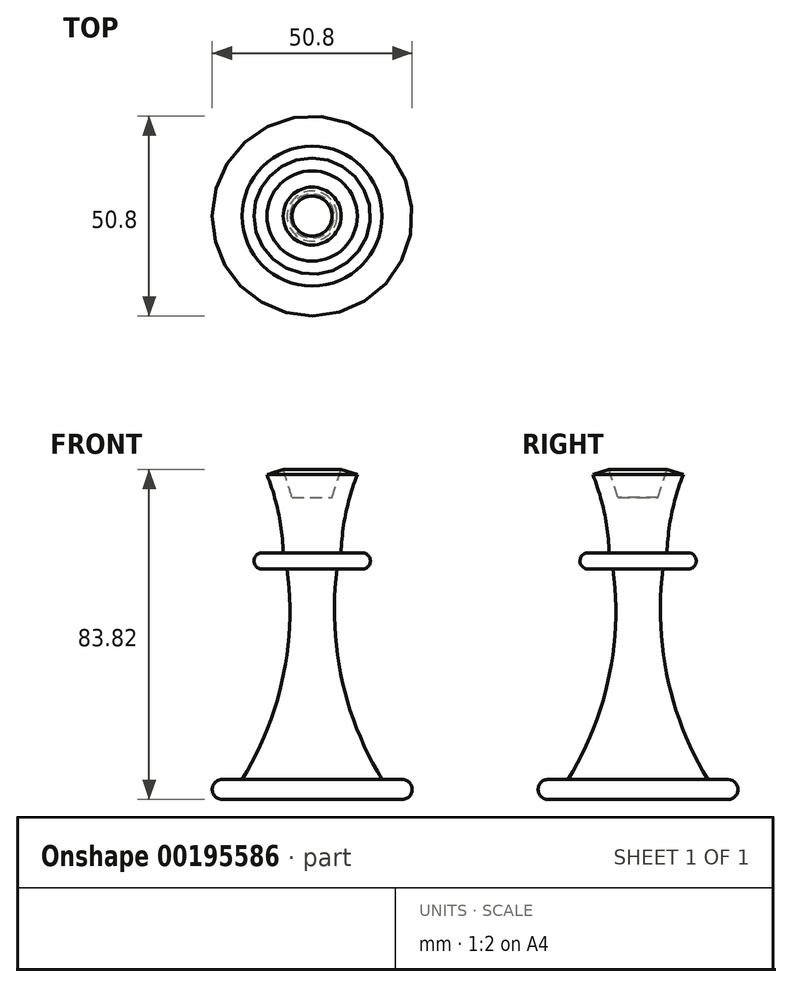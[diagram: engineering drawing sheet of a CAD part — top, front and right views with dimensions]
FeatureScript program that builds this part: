
annotation { "Feature Type Name" : "Feature", "Feature Type Description" : "" }
export const myFeature = defineFeature(function(context is Context, id is Id, definition is map)
    precondition{}
    {
        {
            var Q0;
            Q0=qCreatedBy(makeId("Front.planeOp"),FACE);
            var sketch = newSketch(context, id + "F0", { "sketchPlane" : qUnion([Q0])});
            skLineSegment(sketch, "E0", {"start": v(0, 0) * mm, "end": v(0, 83.82) * mm});
            skLineSegment(sketch, "E1", {"start": v(0, 0) * mm, "end": v(22.86, 0) * mm});
            skLineSegment(sketch, "E2", {"start": v(22.86, 5.08) * mm, "end": v(17.78, 5.08) * mm});
            skLineSegment(sketch, "E3", {"start": v(0, 76.68) * mm, "end": v(5.08, 76.68) * mm});
            skLineSegment(sketch, "E4", {"start": v(5.08, 76.68) * mm, "end": v(7.36, 83.82) * mm});
            skLineSegment(sketch, "E5", {"start": v(7.36, 83.82) * mm, "end": v(11.47, 82.5) * mm});
            skLineSegment(sketch, "E6", {"start": v(7.36, 62.68) * mm, "end": v(12.7, 62.68) * mm});
            skLineSegment(sketch, "E7", {"start": v(12.7, 58.5) * mm, "end": v(6.35, 58.5) * mm});
            skArc(sketch, "E8", {"start": v(11.47, 82.5) * mm, "mid": v(8.56, 72.77) * mm, "end": v(7.36, 62.68) * mm});
            skArc(sketch, "E9", {"start": v(6.35, 58.5) * mm, "mid": v(7.47, 30.8) * mm, "end": v(17.78, 5.08) * mm});
            skPoint(sketch, "E10.orphan", {"position": v(0, 58.5) * mm});
            skArc(sketch, "E11", {"start": v(12.7, 58.5) * mm, "mid": v(14.79, 60.59) * mm, "end": v(12.7, 62.68) * mm});
            skArc(sketch, "E12", {"start": v(22.86, 0) * mm, "mid": v(25.4, 2.54) * mm, "end": v(22.86, 5.08) * mm});
            skSolve(sketch);
        }
        {
            var Q0;
            {var subQ0=sQuery(id+"F0.wireOp",EDGE,"E1");Q0=makeQuery(id+"F0.imprint","IMPRINT",FACE,{"disambiguationData":[TD([[makeQuery(id+"F0.imprint","IMPRINT",EDGE,{"derivedFrom":subQ0}),1.0]])]});}
            var Q1;
            Q1=sQuery(id+"F0.wireOp",EDGE,"E0");
            revolve(context, id + "F1", {"entities" : qUnion([Q0]), "axis" : qUnion([Q1]), "revolveType" : RevolveType.FULL});
        }
    });
